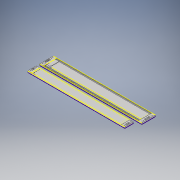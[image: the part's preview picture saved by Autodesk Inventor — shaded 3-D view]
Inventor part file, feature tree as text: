
AUTODESK INVENTOR PART (.ipt)
format: ipt  version: 2018 (Build 220112000, 112)  size: 295,936 bytes
history: native  units: in
note: dims shown in document units (in); Inventor stores cm internally (conversion verified against a paired STEP export)
features: extrude x6, other x5, hole x1, plane x1
ambient origin geometry x8: Origin, YZ Plane, XZ Plane, XY Plane, X Axis, Y Axis, Z Axis, Center Point
bodies: Solid1 (feature_tree)
feature tree (13):
  other  "Base Sketch"
  extrude  "Lower Level"  Depth=60.0in
  extrude  "Base"  Depth=8.0in
  other  "Handles Sketch"
  extrude  "Extrusion3"  Depth=2.0in
  hole  "Hole1"  [1 undecoded]
  plane  "Work Plane1"
  other  "Pocket Level Sketch"
  extrude  "Bed Cut"  Depth=0.75in
  extrude  "Tracks Cut"  Depth=1.0in
  other  "Origin Sketch"
  extrude  "Registration Hole"  Depth=0.75in
  other  "Registration Sketch"
note: 1 required parameter value undecoded (feature->parameter linkage not recoverable at this tier; creation-order binding heuristic only, values carry confidence <= 0.55)
